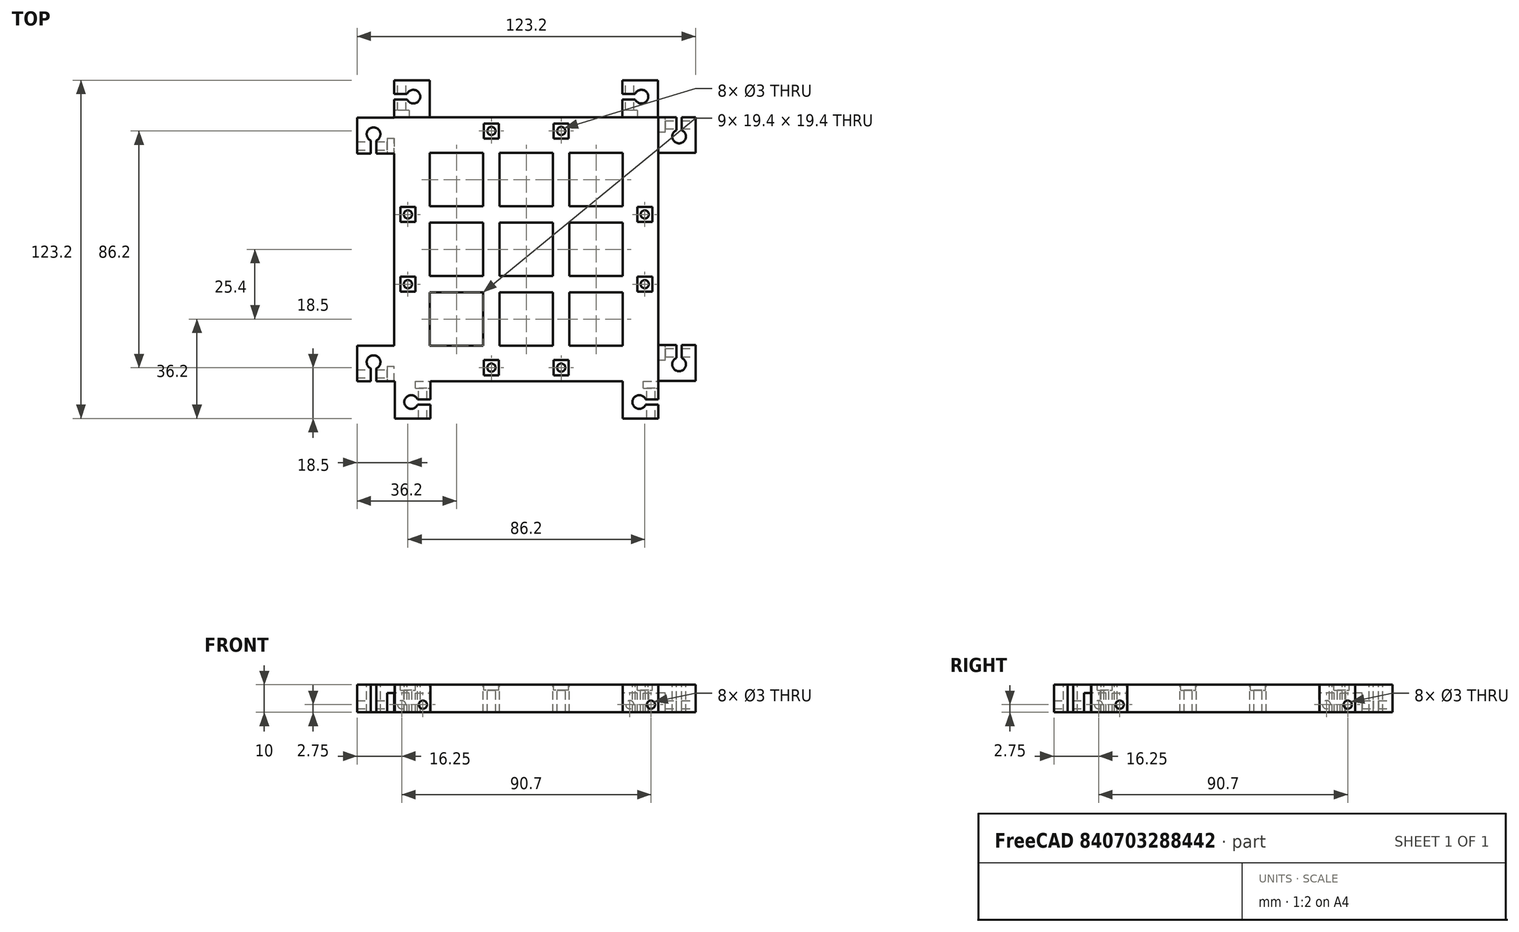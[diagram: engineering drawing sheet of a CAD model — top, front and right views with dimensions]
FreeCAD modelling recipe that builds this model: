
FCSTD DOCUMENT
Label: base
objects: Part::Cut×28, Part::Box×13, Part::Cylinder×10, Part::MultiFuse×8, App::MeasureDistance×2
note: 59 computed .brp shape members not serialized (recipe doc carries the construction recipe); baked Part::Feature solids carry a one-line shape summary decoded from their .brp

FEATURE [Part::Box] Box
  Height = 10
  Length = 96.2
  Width = 96.2
FEATURE [Part::Box] Box001
  Height = 10
  Length = 19.4
  Placement = pos=(13,13,0) rot=(0,0,1;0rad)
  Width = 19.4
FEATURE [Part::Box] Box001002
  Height = 10
  Length = 19.4
  Placement = pos=(63.8,13,0) rot=(0,0,1;0rad)
  Width = 19.4
FEATURE [Part::Box] Box001003
  Height = 10
  Length = 19.4
  Placement = pos=(13,38.4,0) rot=(0,0,1;0rad)
  Width = 19.4
FEATURE [Part::Box] Box001004
  Height = 10
  Length = 19.4
  Placement = pos=(38.4,38.4,0) rot=(0,0,1;0rad)
  Width = 19.4
FEATURE [Part::Box] Box001005
  Height = 10
  Length = 19.4
  Placement = pos=(63.8,38.4,0) rot=(0,0,1;0rad)
  Width = 19.4
FEATURE [Part::Box] Box001006
  Height = 10
  Length = 19.4
  Placement = pos=(63.8,63.8,0) rot=(0,0,1;0rad)
  Width = 19.4
FEATURE [Part::Box] Box001007
  Height = 10
  Length = 19.4
  Placement = pos=(13,63.8,0) rot=(0,0,1;0rad)
  Width = 19.4
FEATURE [Part::Box] Box001008
  Height = 10
  Length = 19.4
  Placement = pos=(38.4,63.8,0) rot=(0,0,1;0rad)
  Width = 19.4
FEATURE [Part::Cut] Cut
  Base = -> Box
  Tool = -> Box001
FEATURE [Part::Cut] Cut001
  Base = -> Cut
  Tool = -> Box001008
FEATURE [Part::Cut] Cut002
  Base = -> Cut001
  Tool = -> Box001007
FEATURE [Part::Cut] Cut003
  Base = -> Cut002
  Tool = -> Box001006
FEATURE [Part::Cut] Cut004
  Base = -> Cut003
  Tool = -> Box001005
FEATURE [Part::Cut] Cut005
  Base = -> Cut004
  Tool = -> Box001004
FEATURE [Part::Cut] Cut006
  Base = -> Cut005
  Tool = -> Box001003
FEATURE [Part::Cut] Cut007
  Base = -> Cut006
  Tool = -> Box001002
FEATURE [Part::Cut] Cut012
  Placement = pos=(0,96,0) rot=(0,0,-1;1.5708rad)
FEATURE [Part::Cut] Cut008
  Base = -> Cut007
FEATURE [Part::Cut] Cut015
  Placement = pos=(83.2,0,0) rot=(0,0,1;0rad)
FEATURE [Part::Cut] Cut017
  Placement = pos=(96.2,83.2,0) rot=(0,0,1;1.5708rad)
FEATURE [Part::Cut] Cut019
  Placement = pos=(13,96.2,0) rot=(0,0,1;3.14159rad)
FEATURE [Part::Cut] Cut012001
  Placement = pos=(0,13,0) rot=(0,0,-1;1.5708rad)
FEATURE [Part::Cut] Cut012001001
  Placement = pos=(0.2,0,0) rot=(0,0,1;0rad)
FEATURE [Part::Cut] Cut015001
  Placement = pos=(96.2,0.2,0) rot=(0,0,1;1.5708rad)
FEATURE [Part::Cut] Cut017001
  Placement = pos=(96,96.2,0) rot=(0,0,1;3.14159rad)
FEATURE [Part::Cylinder] Cylinder001
  Angle = 360
  Height = 12
  Placement = pos=(-14,85.75,2.75) rot=(0,1,0;1.5708rad)
  Radius = 1.5
FEATURE [Part::Cylinder] Cylinder
  Angle = 360
  Height = 12
  Placement = pos=(-14,2.75,2.75) rot=(0,1,0;1.5708rad)
  Radius = 1.5
FEATURE [Part::Cylinder] Cylinder001001
  Angle = 360
  Height = 12
  Placement = pos=(98,93.45,2.75) rot=(0,1,0;1.5708rad)
  Radius = 1.5
FEATURE [Part::Cylinder] Cylinder001001001
  Angle = 360
  Height = 12
  Placement = pos=(98,10.45,2.75) rot=(0,1,0;1.5708rad)
  Radius = 1.5
FEATURE [Part::Cylinder] Cylinder001001001001
  Angle = 360
  Height = 12
  Placement = pos=(93.45,-14.25,2.75) rot=(-1,0,0;1.5708rad)
  Radius = 1.5
FEATURE [Part::Cylinder] Cylinder001001001001001
  Angle = 360
  Height = 12
  Placement = pos=(10.45,-14.25,2.75) rot=(-1,0,0;1.5708rad)
  Radius = 1.5
FEATURE [Part::Cylinder] Cylinder001001001001001001
  Angle = 360
  Height = 12
  Placement = pos=(2.75,97.75,2.75) rot=(-1,0,0;1.5708rad)
  Radius = 1.5
FEATURE [Part::Cylinder] Cylinder001001001001001001001
  Angle = 360
  Height = 12
  Placement = pos=(85.75,97.75,2.75) rot=(-1,0,0;1.5708rad)
  Radius = 1.5
FEATURE [Part::Box] Box001009
  Height = 2
  Length = 5.5
  Placement = pos=(2.25,32.65,8) rot=(0,0,1;0rad)
  Width = 5.5
FEATURE [Part::Box] Box001009001
  Height = 2
  Length = 5.5
  Placement = pos=(88.45,58.05,8) rot=(0,0,1;0rad)
  Width = 5.5
FEATURE [Part::Box] Box001009002
  Height = 2
  Length = 5.5
  Placement = pos=(88.45,32.65,8) rot=(0,0,1;0rad)
  Width = 5.5
FEATURE [Part::Box] Box001009001001
  Height = 2
  Length = 5.5
  Placement = pos=(2.25,58.05,8) rot=(0,0,1;0rad)
  Width = 5.5
FEATURE [Part::MultiFuse] Fusion
  Shapes = -> [Box001009001001,Box001009,Box001009001,Box001009002]
FEATURE [Part::MultiFuse] Fusion001
  Placement = pos=(96.2,0,0) rot=(0,0,1;1.5708rad)
  Shapes = -> [Box001009001001,Box001009,Box001009001,Box001009002]
FEATURE [Part::MultiFuse] Fusion002
  Shapes = -> [Cut017001,Cut012,Cut008,Cut015,Cut017,Cut019,Cut012001,Cut012001001,Cut015001]
FEATURE [Part::Cut] Cut012001002
  Base = -> Fusion002
  Tool = -> Cylinder001
FEATURE [Part::Cut] Cut012001003
  Base = -> Cut012001002
  Tool = -> Cylinder001001001001001001001
FEATURE [Part::Cut] Cut012001004
  Base = -> Cut012001003
  Tool = -> Cylinder001001001001001001
FEATURE [Part::Cut] Cut012001005
  Base = -> Cut012001004
  Tool = -> Cylinder001001001001001
FEATURE [Part::Cut] Cut012001006
  Base = -> Cut012001005
  Tool = -> Cylinder001001001001
FEATURE [Part::Cut] Cut012001007
  Base = -> Cut012001006
  Tool = -> Cylinder001001001
FEATURE [Part::Cut] Cut012001008
  Base = -> Cut012001007
  Tool = -> Cylinder001001
FEATURE [Part::Cut] Cut012001009
  Base = -> Cut012001008
  Tool = -> Cylinder
FEATURE [Part::Cut] Cut012001010
  Base = -> Cut012001009
  Tool = -> Fusion001
FEATURE [Part::Cut] Cut012001011
  Base = -> Cut012001010
  Tool = -> Fusion
FEATURE [Part::Cylinder] Cylinder001001001001001001002
  Angle = 360
  Height = 10
  Placement = pos=(5,35.4,0) rot=(0,0,1;0rad)
  Radius = 1.5
FEATURE [Part::Cylinder] Cylinder001001001001001001002001
  Angle = 360
  Height = 10
  Placement = pos=(5,60.8,0) rot=(0,0,1;0rad)
  Radius = 1.5
FEATURE [Part::MultiFuse] Fusion003
  Shapes = -> [Cylinder001001001001001001002001,Cylinder001001001001001001002]
FEATURE [Part::MultiFuse] Fusion003001
  Placement = pos=(86.2,0,0) rot=(0,0,1;0rad)
  Shapes = -> [Cylinder001001001001001001002001,Cylinder001001001001001001002]
FEATURE [Part::MultiFuse] Fusion003002
  Shapes = -> [Fusion003,Fusion003001]
FEATURE [Part::MultiFuse] Fusion003002001
  Placement = pos=(96.2,0,0) rot=(0,0,1;1.5708rad)
  Shapes = -> [Fusion003,Fusion003001]
FEATURE [Part::MultiFuse] Fusion003002002
  Shapes = -> [Fusion003002,Fusion003002001]
FEATURE [Part::Cut] Cut012001012
  Base = -> Cut012001011
  Tool = -> Fusion003002002
FEATURE [App::MeasureDistance] Distance  label="Distance: 3.721"
  Distance = 3.72117
  P1 = (8.4492,99.1298,10)
  P2 = (9.31226,102.75,10)
FEATURE [App::MeasureDistance] Distance001  label="Distance: 85.467"
  Distance = 83.0005
  P1 = (7,103.69,10)
  P2 = (90,103.4,10)
